FCSTD DOCUMENT  (FreeCAD 0.19R24366 (Git))
Label: layens-data
License: Creative Commons Attribution-NonCommercial-ShareAlike
LicenseURL: http://creativecommons.org/licenses/by-nc-sa/4.0/
objects: Spreadsheet::Sheet×1

FEATURE [Spreadsheet::Sheet] Spreadsheet
  cells = A1=name; B1=value; A2=frame_topbar_x; B2(frame_topbar_x)==363.54mm; A3=frame_topbar_y; B3(frame_topbar_y)==38.1mm; A4=frame_topbar_z; B4(frame_topbar_z)==19.05mm; A5=frame_topbar_shoulder_depth; B5(frame_topbar_shoulder_depth)==9.525mm; A6=frame_topbar_shoulder_x; B6(frame_topbar_shoulder_x)==26.99mm; A7=frame_side_x; B7(frame_side_x)==25.4mm; A8=frame_side_y; B8(frame_side_y)==385.76mm; A9=frame_side_z; B9(frame_side_z)==9.529999999999999mm; A10=bottom_bar_x; B10(bottom_bar_x)==309.56mm; A11=bottom_bar_y; B11(bottom_bar_y)==19.05mm; A12=bottom_bar_z; B12(bottom_bar_z)==19.05mm; A14=hive_frame_clearance; B14(hive_frame_clearance)==3.17mm; C14=clearance between frame sidebars and inside frame y direction; A15=hive_insulation_thickness; B15(hive_insulation_thickness)==152.4mm; A16=hive_number_of_frames; B16(hive_number_of_frames)=40; A17=hive_plywood_thickness; B17(hive_plywood_thickness)==12.7mm; A18=hive_inside_x; B18(hive_inside_x)==frame_topbar_z * hive_number_of_frames + 2 * hive_plywood_thickness; A19=hive_inside_y; B19(hive_inside_y)==bottom_bar_x + 2 * (frame_side_z + hive_frame_clearance); A20=hive_outside_x; B20(hive_outside_x)==hive_inside_x + 2 * (hive_insulation_thickness + 2 * hive_plywood_thickness); A21=hive_outside_y; B21(hive_outside_y)==hive_inside_y + 2 * (hive_insulation_thickness + 2 * hive_plywood_thickness); A22=hive_bottom_frame_clearance; B22(hive_bottom_frame_clearance)==25.4mm; A23=hive_inside_z; B23(hive_inside_z)==frame_side_y + hive_bottom_frame_clearance; A24=lid_overhang; B24(lid_overhang)==200mm; A25=neoprene_gasket_thickness; B25(neoprene_gasket_thickness)==10mm
